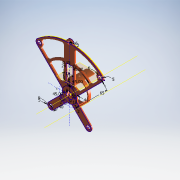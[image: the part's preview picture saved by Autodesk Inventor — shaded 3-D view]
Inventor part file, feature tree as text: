
AUTODESK INVENTOR PART (.ipt)
format: ipt  version: 2018.2 (Build 222227000, 227)  size: 373,760 bytes
history: native  units: mm
features: extrude x8, thread x7, sketch x4, plane x3, mirror x2, fillet x2, revolve x1
ambient origin geometry x8: Origin, YZ Plane, XZ Plane, XY Plane, X Axis, Y Axis, Z Axis, Center Point
bodies: Solid1 (feature_tree)
feature tree (27):
  extrude  "Extrusion1"  Depth=10.0mm
  extrude  "Extrusion3"  Depth=8.0mm
  extrude  "Extrusion4"  Depth=8.0mm
  revolve  "Revolution1"  [1 undecoded]
  plane  "Work Plane1"
  extrude  "Extrusion5"  Depth=2.0mm
  plane  "Work Plane4"
  extrude  "Extrusion6"  Depth=10.0mm
  mirror  "Mirror1"
  extrude  "Extrusion8"  TaperAngle=45.0deg  [1 undecoded]
  fillet  "Fillet4"  Radius=32.0mm
  mirror  "Mirror2"
  sketch  "Sketch8"  dims[d7=2.0mm d8=0.0mm d10=4.0mm d14=2.0mm d15=6.0mm d16=45.0deg d17=32.0mm d18=0.0mm d23=16.0mm d24=0.0mm d25=4.0mm d26=90.0deg d33=3.0mm d34=3.0mm d35=3.0mm d36=8.0mm d38=8.0mm d40=10.0mm d41=0.0mm d44=3.0mm d45=10.0mm d46=0.0mm d47=10.0mm d48=11.0mm d56=0.15mm d57=0.15mm d58=24.0mm d61=45.0deg d62=40.0mm d63=5.0mm d64=6.0mm d65=2.0mm d66=2.0mm d67=45.0deg d68=12.0mm d69=45.0deg d70=65.0mm d71=6.0mm d72=5.0mm d73=8.0mm d74=3.0mm d75=3.0mm d76=3.0mm d77=3.0mm d78=2.0mm d79=10.0mm d80=0.0mm d81=3.0mm d82=6.0mm d84=2.0mm d85=10.0mm d86=0.0mm d87=10.0mm d88=0.0mm d89=3.0mm d90=10.0mm d91=0.0mm d92=10.0mm d93=0.0mm d94=10.0mm d95=0.0mm d96=10.0mm d97=0.0mm d98=10.0mm d99=0.0mm d100=10.0mm d101=0.0mm d102=10.0mm d103=0.0mm]
  extrude  "Extrusion9"  Depth=16.0mm TaperAngle=0.0deg
  extrude  "Extrusion10"  Depth=4.0mm
  fillet  "Fillet5"  [1 undecoded]
  thread  "Thread1"  [1 undecoded]
  thread  "Thread2"  [1 undecoded]
  thread  "Thread3"  [1 undecoded]
  thread  "Thread4"  [1 undecoded]
  thread  "Thread5"  [1 undecoded]
  thread  "Thread6"  [1 undecoded]
  thread  "Thread7"  [1 undecoded]
  sketch  "Sketch2"  dims[d0=10.0mm d1=0.15mm]
  plane  "Work Plane3"
  sketch  "Sketch4"  dims[d2=2.5mm d4=8.0mm]
  sketch  "Sketch7"  dims[d5=8.0mm d6=22.0mm]
note: 10 required parameter values undecoded (feature->parameter linkage not recoverable at this tier; creation-order binding heuristic only, values carry confidence <= 0.55)